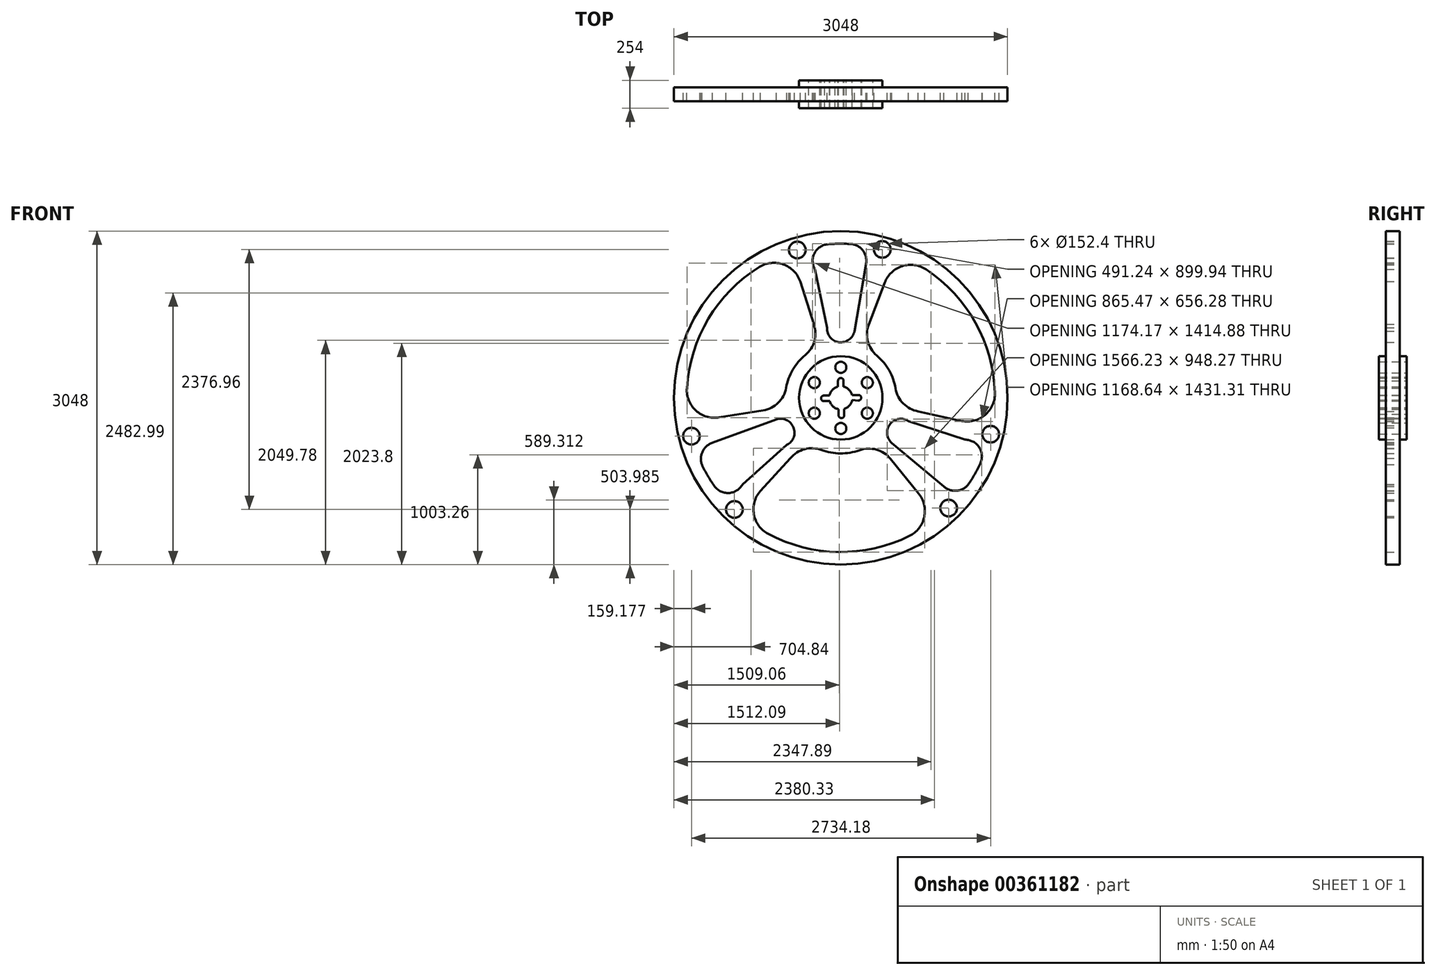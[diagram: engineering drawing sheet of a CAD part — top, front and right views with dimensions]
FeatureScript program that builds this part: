
annotation { "Feature Type Name" : "Feature", "Feature Type Description" : "" }
export const myFeature = defineFeature(function(context is Context, id is Id, definition is map)
    precondition{}
    {
        {
            var Q0;
            Q0=qCreatedBy(makeId("Front.planeOp"),FACE);
            var sketch = newSketch(context, id + "F0", { "sketchPlane" : qUnion([Q0])});
            skCircle(sketch, "E0", {"center": v(0, 0) * mm, "radius": 1524 * mm});
            skArc(sketch, "E1", {"start": v(-469.86, 1328.32) * mm, "mid": v(-477.5, 1325.6) * mm, "end": v(-485.13, 1322.82) * mm});
            skArc(sketch, "E2", {"start": v(-118, 1404.02) * mm, "mid": v(-241.07, 1321.27) * mm, "end": v(-235.51, 1173.07) * mm});
            skArc(sketch, "E3", {"start": v(230.6, 1221.2) * mm, "mid": v(207, 1339.25) * mm, "end": v(106.11, 1404.97) * mm});
            skArc(sketch, "E4", {"start": v(-323.89, 391.36) * mm, "mid": v(-438.34, 256.76) * mm, "end": v(-499.76, 91.1) * mm});
            skPoint(sketch, "E5.centerSnap0", {"position": v(-151.92, 764.42) * mm});
            skArc(sketch, "E6", {"start": v(-126.32, 641.29) * mm, "mid": v(-16.05, 509.02) * mm, "end": v(123.96, 609.28) * mm});
            skArc(sketch, "E7.trimOffspring", {"start": v(106.11, 1404.97) * mm, "mid": v(-5.96, 1408.96) * mm, "end": v(-118, 1404.02) * mm});
            skLineSegment(sketch, "E8.trimOffspring", {"start": v(123.96, 609.28) * mm, "end": v(230.6, 1221.2) * mm});
            skLineSegment(sketch, "E9.trimOffspring", {"start": v(-126.32, 641.29) * mm, "end": v(-235.51, 1173.07) * mm});
            skCircle(sketch, "E10", {"center": v(-397.36, 1351.78) * mm, "radius": 76.2 * mm});
            skCircle(sketch, "E11", {"center": v(379.35, 1356.94) * mm, "radius": 76.2 * mm});
            skArc(sketch, "E12.1.0", {"start": v(-1269.8, -610.59) * mm, "mid": v(-1217.21, -709.64) * mm, "end": v(-1156.92, -804.2) * mm});
            skArc(sketch, "E12.1.1", {"start": v(-1172.88, -410.9) * mm, "mid": v(-1263.32, -490.37) * mm, "end": v(-1269.8, -610.59) * mm});
            skLineSegment(sketch, "E12.1.2", {"start": v(-589.63, -197.29) * mm, "end": v(-1172.88, -410.9) * mm});
            skArc(sketch, "E12.1.3", {"start": v(-492.21, -430.04) * mm, "mid": v(-432.8, -268.4) * mm, "end": v(-589.63, -197.29) * mm});
            skPoint(sketch, "E12.1.4", {"position": v(-586.04, -513.77) * mm});
            skArc(sketch, "E12.1.5", {"start": v(-1156.92, -804.2) * mm, "mid": v(-1023.71, -869.4) * mm, "end": v(-898.15, -790.5) * mm});
            skLineSegment(sketch, "E12.1.6", {"start": v(-492.21, -430.04) * mm, "end": v(-898.15, -790.5) * mm});
            skCircle(sketch, "E12.1.7", {"center": v(-972, -1020.02) * mm, "radius": 76.2 * mm});
            skCircle(sketch, "E12.1.8", {"center": v(-1364.82, -349.94) * mm, "radius": 76.2 * mm});
            skArc(sketch, "E12.2.0", {"start": v(1163.68, -794.38) * mm, "mid": v(1223.18, -699.32) * mm, "end": v(1274.92, -599.82) * mm});
            skArc(sketch, "E12.2.1", {"start": v(942.29, -810.3) * mm, "mid": v(1056.33, -848.89) * mm, "end": v(1163.68, -794.38) * mm});
            skLineSegment(sketch, "E12.2.2", {"start": v(465.67, -412) * mm, "end": v(942.29, -810.3) * mm});
            skArc(sketch, "E12.2.3", {"start": v(618.53, -211.25) * mm, "mid": v(448.85, -240.61) * mm, "end": v(465.67, -412) * mm});
            skPoint(sketch, "E12.2.4", {"position": v(737.96, -250.64) * mm});
            skArc(sketch, "E12.2.5", {"start": v(1274.92, -599.82) * mm, "mid": v(1264.78, -451.86) * mm, "end": v(1133.66, -382.58) * mm});
            skLineSegment(sketch, "E12.2.6", {"start": v(618.53, -211.25) * mm, "end": v(1133.66, -382.58) * mm});
            skCircle(sketch, "E12.2.7", {"center": v(1369.36, -331.76) * mm, "radius": 76.2 * mm});
            skCircle(sketch, "E12.2.8", {"center": v(985.47, -1007) * mm, "radius": 76.2 * mm});
            skArc(sketch, "E13", {"start": v(-370.07, 1063.85) * mm, "mid": v(-525.28, 1220.13) * mm, "end": v(-744.24, 1196.37) * mm});
            skArc(sketch, "E14", {"start": v(-1406.25, 87.6) * mm, "mid": v(-1323.4, -116.32) * mm, "end": v(-1112.4, -178.97) * mm});
            skArc(sketch, "E15", {"start": v(-323.89, 391.36) * mm, "mid": v(-240.63, 520.76) * mm, "end": v(-247.36, 674.5) * mm});
            skArc(sketch, "E16", {"start": v(-709.3, -114.12) * mm, "mid": v(-571.92, -44.8) * mm, "end": v(-499.76, 91.1) * mm});
            skArc(sketch, "E17.trimOffspring", {"start": v(-744.24, 1196.37) * mm, "mid": v(-1209.75, 722.3) * mm, "end": v(-1406.25, 87.6) * mm});
            skLineSegment(sketch, "E18.trimOffspring", {"start": v(-247.36, 674.5) * mm, "end": v(-370.07, 1063.85) * mm});
            skLineSegment(sketch, "E19.trimOffspring", {"start": v(-709.3, -114.12) * mm, "end": v(-1112.4, -178.97) * mm});
            skArc(sketch, "E20.1.0", {"start": v(-663.97, -1242.72) * mm, "mid": v(-20.65, -1408.82) * mm, "end": v(627.26, -1261.64) * mm});
            skArc(sketch, "E20.1.1", {"start": v(-736.29, -852.42) * mm, "mid": v(-794.02, -1064.97) * mm, "end": v(-663.97, -1242.72) * mm});
            skLineSegment(sketch, "E20.1.2", {"start": v(-460.45, -551.47) * mm, "end": v(-736.29, -852.42) * mm});
            skArc(sketch, "E20.1.3", {"start": v(-176.98, -476.17) * mm, "mid": v(-330.68, -468.77) * mm, "end": v(-460.45, -551.47) * mm});
            skArc(sketch, "E20.1.4", {"start": v(453.48, -557.21) * mm, "mid": v(324.76, -472.9) * mm, "end": v(170.98, -478.36) * mm});
            skLineSegment(sketch, "E20.1.5", {"start": v(453.48, -557.21) * mm, "end": v(711.19, -873.87) * mm});
            skArc(sketch, "E20.1.6", {"start": v(627.26, -1261.64) * mm, "mid": v(762.44, -1087.93) * mm, "end": v(711.19, -873.87) * mm});
            skArc(sketch, "E20.2.0", {"start": v(1408.2, 46.35) * mm, "mid": v(1230.4, 686.53) * mm, "end": v(778.98, 1174.05) * mm});
            skArc(sketch, "E20.2.1", {"start": v(1106.36, -211.44) * mm, "mid": v(1319.3, -155.16) * mm, "end": v(1408.2, 46.35) * mm});
            skLineSegment(sketch, "E20.2.2", {"start": v(707.8, -123.02) * mm, "end": v(1106.36, -211.44) * mm});
            skArc(sketch, "E20.2.3", {"start": v(500.87, 84.82) * mm, "mid": v(571.3, -52) * mm, "end": v(707.8, -123.02) * mm});
            skArc(sketch, "E20.2.4", {"start": v(255.82, 671.33) * mm, "mid": v(247.16, 517.7) * mm, "end": v(328.78, 387.26) * mm});
            skLineSegment(sketch, "E20.2.5", {"start": v(255.82, 671.33) * mm, "end": v(401.2, 1052.84) * mm});
            skArc(sketch, "E20.2.6", {"start": v(778.98, 1174.05) * mm, "mid": v(560.96, 1204.26) * mm, "end": v(401.2, 1052.84) * mm});
            skArc(sketch, "E21.trimOffspring", {"start": v(500.87, 84.82) * mm, "mid": v(441.53, 251.23) * mm, "end": v(328.78, 387.26) * mm});
            skArc(sketch, "E22.trimOffspring", {"start": v(-176.98, -476.17) * mm, "mid": v(-3.2, -507.99) * mm, "end": v(170.98, -478.36) * mm});
            skCircle(sketch, "E23", {"center": v(0, 0) * mm, "radius": 381 * mm});
            skCircle(sketch, "E24", {"center": v(0, 279.4) * mm, "radius": 50.8 * mm});
            skCircle(sketch, "E25.1.0", {"center": v(-241.97, -139.7) * mm, "radius": 50.8 * mm});
            skCircle(sketch, "E25.2.0", {"center": v(241.97, -139.7) * mm, "radius": 50.8 * mm});
            skCircle(sketch, "E26", {"center": v(-241.97, 139.7) * mm, "radius": 50.8 * mm});
            skCircle(sketch, "E27.1.0", {"center": v(0, -279.4) * mm, "radius": 50.8 * mm});
            skCircle(sketch, "E27.2.0", {"center": v(241.97, 139.7) * mm, "radius": 50.8 * mm});
            skArc(sketch, "E28", {"start": v(-101.47, -29.1) * mm, "mid": v(-71.15, -77.98) * mm, "end": v(-19.69, -103.71) * mm});
            skArc(sketch, "E29", {"start": v(25.38, 155.25) * mm, "mid": v(0.56, 181.76) * mm, "end": v(-25.4, 156.36) * mm});
            skArc(sketch, "E30.1.0", {"start": v(-155.1, 20.95) * mm, "mid": v(-180.31, -7.56) * mm, "end": v(-148.94, -29.1) * mm});
            skArc(sketch, "E30.2.0", {"start": v(-19.69, -159.55) * mm, "mid": v(11, -184.4) * mm, "end": v(28.92, -149.22) * mm});
            skArc(sketch, "E30.3.0", {"start": v(159, -24.07) * mm, "mid": v(186.2, 0.35) * mm, "end": v(160.82, 26.66) * mm});
            skPoint(sketch, "E30.center", {"position": v(2.86, -1.6) * mm});
            skLineSegment(sketch, "E31", {"start": v(25.38, 155.25) * mm, "end": v(25.38, 102.47) * mm});
            skLineSegment(sketch, "E32", {"start": v(-25.4, 156.36) * mm, "end": v(-25.4, 102.46) * mm});
            skLineSegment(sketch, "E33", {"start": v(-155.1, 20.95) * mm, "end": v(-103.46, 20.95) * mm});
            skLineSegment(sketch, "E34", {"start": v(-148.94, -29.1) * mm, "end": v(-101.47, -29.1) * mm});
            skLineSegment(sketch, "E35", {"start": v(-19.69, -159.55) * mm, "end": v(-19.69, -103.71) * mm});
            skLineSegment(sketch, "E36", {"start": v(28.92, -149.22) * mm, "end": v(28.92, -101.52) * mm});
            skLineSegment(sketch, "E37", {"start": v(160.82, 26.66) * mm, "end": v(102.14, 26.66) * mm});
            skLineSegment(sketch, "E38", {"start": v(159, -24.07) * mm, "end": v(103.63, -20.1) * mm});
            skArc(sketch, "E39.trimOffspring", {"start": v(-25.4, 102.46) * mm, "mid": v(-76.24, 73.01) * mm, "end": v(-103.46, 20.95) * mm});
            skArc(sketch, "E40.trimOffspring", {"start": v(102.14, 26.66) * mm, "mid": v(74.17, 75.11) * mm, "end": v(25.38, 102.47) * mm});
            skArc(sketch, "E41.trimOffspring", {"start": v(28.92, -101.52) * mm, "mid": v(77.78, -71.37) * mm, "end": v(103.63, -20.1) * mm});
            skSolve(sketch);
        }
        {
            var Q0;
            Q0=makeQuery(id+"F0.imprint","IMPRINT",FACE,{"disambiguationData":[TD([[makeQuery(id+"F0.imprint","IMPRINT",EDGE,{"derivedFrom":sQuery(id+"F0.wireOp",EDGE,"E0")}),1.0]])]});
            extrude(context, id + "F1", {"entities" : qUnion([Q0]), "depth" : 127 * mm, "symmetric" : true});
        }
        {
            var Q0;
            Q0=makeQuery(id+"F0.imprint","IMPRINT",FACE,{"disambiguationData":[TD([[makeQuery(id+"F0.imprint","IMPRINT",EDGE,{"derivedFrom":sQuery(id+"F0.wireOp",EDGE,"E23")}),1.0]])]});
            extrude(context, id + "F2", {"entities" : qUnion([Q0]), "operationType" : NewBodyOperationType.ADD, "depth" : 254 * mm, "symmetric" : true});
        }
    });
